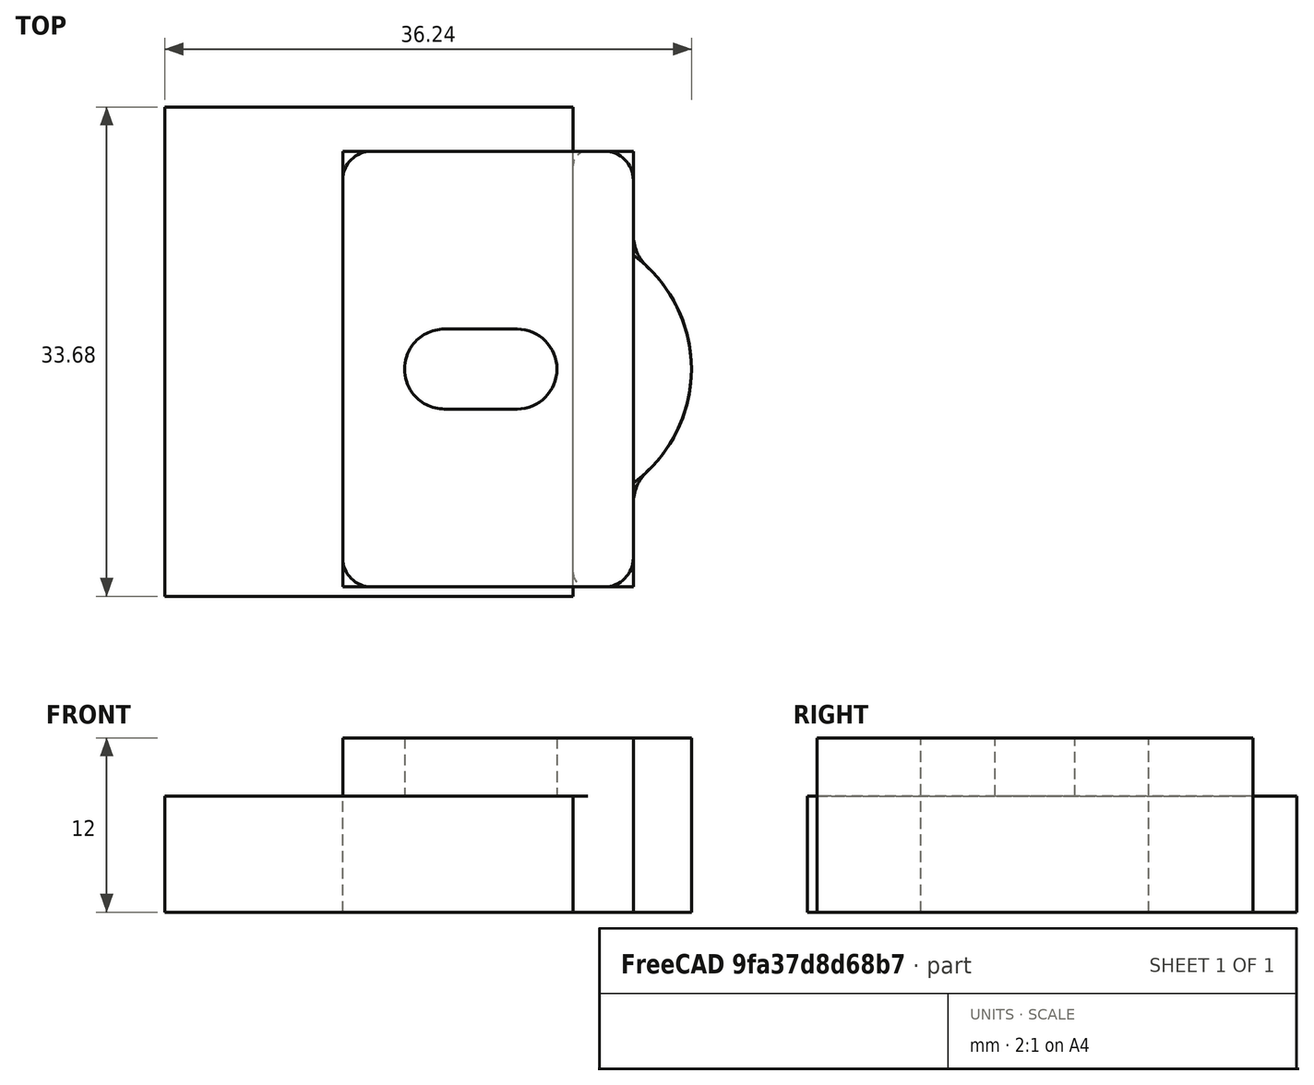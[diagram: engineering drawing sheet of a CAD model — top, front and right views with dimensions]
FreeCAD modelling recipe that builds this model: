
FCSTD DOCUMENT  (FreeCAD 0.16R)
Label: Doorstop
License: All rights reserved
LicenseURL: http://en.wikipedia.org/wiki/All_rights_reserved
objects: Sketcher::SketchObject×4, PartDesign::Fillet×3, PartDesign::Pad×2, PartDesign::Pocket×2, Mesh::Feature×1
note: 15 computed .brp shape members not serialized (recipe doc carries the construction recipe); baked Part::Feature solids carry a one-line shape summary decoded from their .brp

FEATURE [Sketcher::SketchObject] Sketch
  sketch-geometry (4):
    g0: LineSegment StartX=-12 StartY=15 StartZ=0 EndX=8 EndY=15 EndZ=0
    g1: LineSegment StartX=8 StartY=15 StartZ=0 EndX=8 EndY=-15 EndZ=0
    g2: LineSegment StartX=8 StartY=-15 StartZ=0 EndX=-12 EndY=-15 EndZ=0
    g3: LineSegment StartX=-12 StartY=-15 StartZ=0 EndX=-12 EndY=15 EndZ=0
  constraints (12):
    c: Coincident(g0,g1)
    c: Coincident(g1,g2)
    c: Coincident(g2,g3)
    c: Coincident(g3,g0)
    c: Horizontal(g0)
    c: Horizontal(g2)
    c: Vertical(g1)
    c: Vertical(g3)
    c: Distance(g1) = 30
    c: DistanceX(g-2,g0) = 8
    c: Symmetric(g2,g0,g-1)
    c: DistanceX(g0) = -12
FEATURE [PartDesign::Pad] Pad
  Length = 12
  Length2 = 100
  Sketch = -> Sketch
  Type = 0
FEATURE [Sketcher::SketchObject] Sketch001
  ExternalGeometry = -> [Pad]
  Placement = pos=(0,0,12) rot=(0,0,1;0rad)
  Support = -> Pad [Face6]
  sketch-geometry (2):
    g0: Circle CenterX=2.31908 CenterY=0 CenterZ=0 NormalX=0 NormalY=0 NormalZ=1 Radius=9.68092
    g1: LineSegment [constr] StartX=12 StartY=17.47 StartZ=0 EndX=12 EndY=-14.1606 EndZ=0
  constraints (4):
    c: PointOnObject(g0,g-1)
    c: Vertical(g1)
    c: Tangent(g1,g0)
    c: Distance(g1,g-3) = 4
FEATURE [PartDesign::Pad] Pad001
  Length = 12
  Length2 = 100
  Reversed = true
  Sketch = -> Sketch001
  Type = 0
FEATURE [Sketcher::SketchObject] Sketch003
  Placement = pos=(0,0,0) rot=(1,0,0;3.14159rad)
  Support = -> Pad001 [Face4]
  sketch-geometry (4):
    g0: LineSegment StartX=-24.2449 StartY=15.6448 StartZ=0 EndX=3.85394 EndY=15.6448 EndZ=0
    g1: LineSegment StartX=3.85394 StartY=15.6448 StartZ=0 EndX=3.85394 EndY=-18.0419 EndZ=0
    g2: LineSegment StartX=3.85394 StartY=-18.0419 StartZ=0 EndX=-24.2449 EndY=-18.0419 EndZ=0
    g3: LineSegment StartX=-24.2449 StartY=-18.0419 StartZ=0 EndX=-24.2449 EndY=15.6448 EndZ=0
  constraints (8):
    c: Coincident(g0,g1)
    c: Coincident(g1,g2)
    c: Coincident(g2,g3)
    c: Coincident(g3,g0)
    c: Horizontal(g0)
    c: Horizontal(g2)
    c: Vertical(g1)
    c: Vertical(g3)
FEATURE [PartDesign::Pocket] Pocket
  Length = 8
  Sketch = -> Sketch003
  Type = 0
FEATURE [Sketcher::SketchObject] Sketch004
  ExternalGeometry = -> [Pocket]
  Placement = pos=(0,0,8) rot=(1,0,0;3.14159rad)
  Support = -> Pocket [Face2]
  sketch-geometry (4):
    g0: ArcOfCircle CenterX=-5 CenterY=0 CenterZ=0 NormalX=0 NormalY=0 NormalZ=1 Radius=2.75 StartAngle=1.5708 EndAngle=4.71239
    g1: ArcOfCircle CenterX=0 CenterY=0 CenterZ=0 NormalX=0 NormalY=0 NormalZ=1 Radius=2.75 StartAngle=4.71239 EndAngle=7.85398
    g2: LineSegment StartX=-5 StartY=-2.75 StartZ=0 EndX=0 EndY=-2.75 EndZ=0
    g3: LineSegment StartX=-5 StartY=2.75 StartZ=0 EndX=0 EndY=2.75 EndZ=0
  constraints (9):
    c: Tangent(g0,g3) = 1.5708
    c: Tangent(g0,g2) = -1.5708
    c: Tangent(g2,g1) = -1.5708
    c: Tangent(g3,g1) = 1.5708
    c: Horizontal(g2)
    c: Equal(g0,g1)
    c: Distance(g1,g1) = 5.5
    c: Distance(g3) = 5
    c: Coincident(g1,g-1)
FEATURE [PartDesign::Pocket] Pocket001
  Length = 5
  Sketch = -> Sketch004
  Type = 0
FEATURE [PartDesign::Fillet] Fillet
  Base = -> Pocket001 [Edge6,Edge28,Edge30,Edge4]
  Radius = 2
FEATURE [PartDesign::Fillet] Fillet001
  Base = -> Fillet [Edge21,Edge3]
  Radius = 1
FEATURE [PartDesign::Fillet] Fillet002
  Base = -> Fillet001 [Edge42,Edge63]
  Radius = 3
FEATURE [Mesh::Feature] Mesh  label="Fillet002 (Meshed)"
